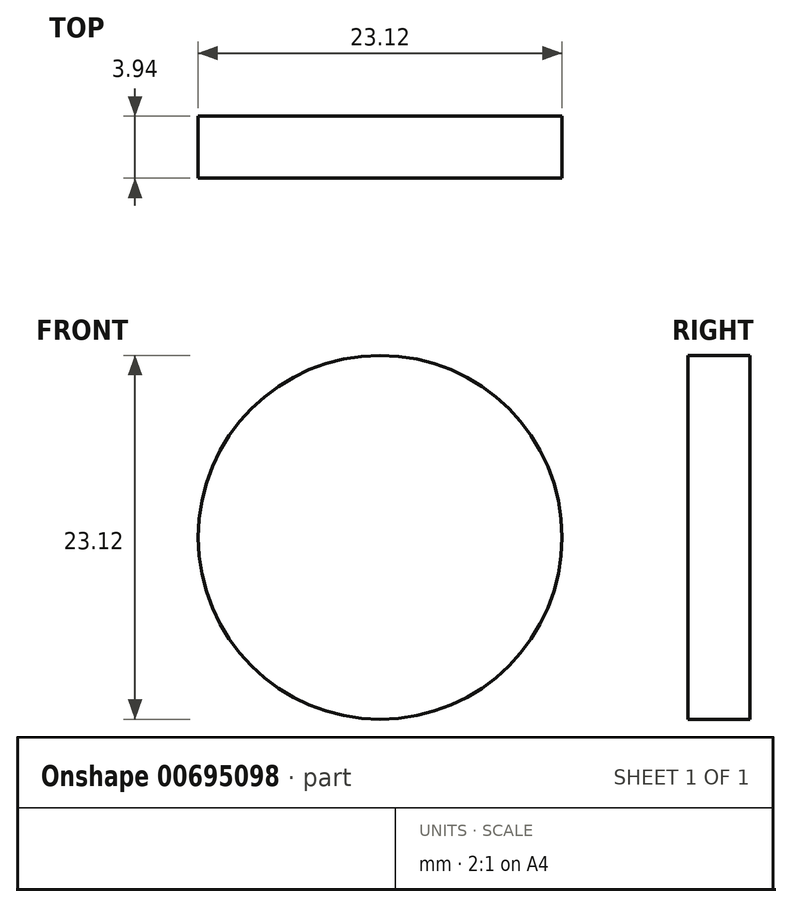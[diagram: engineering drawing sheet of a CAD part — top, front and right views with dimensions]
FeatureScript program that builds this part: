
annotation { "Feature Type Name" : "Feature", "Feature Type Description" : "" }
export const myFeature = defineFeature(function(context is Context, id is Id, definition is map)
    precondition{}
    {
        {
            var Q0;
            Q0=qCreatedBy(makeId("Front.planeOp"),FACE);
            var sketch = newSketch(context, id + "F0", { "sketchPlane" : qUnion([Q0])});
            skCircle(sketch, "E0", {"center": v(0, 0) * mm, "radius": 11.56 * mm});
            skLineSegment(sketch, "E1", {"start": v(0, 0) * mm, "end": v(0, 11.56) * mm});
            skSolve(sketch);
        }
        {
            var Q0;
            Q0=makeQuery(id+"F0.imprint","IMPRINT",FACE,{"disambiguationData":[TD([[makeQuery(id+"F0.imprint","IMPRINT",EDGE,{"derivedFrom":sQuery(id+"F0.wireOp",EDGE,"E0")}),1.0]])]});
            extrude(context, id + "F1", {"entities" : qUnion([Q0]), "depth" : 3.94 * mm, "offsetDistance" : 25.4 * mm});
        }
    });
